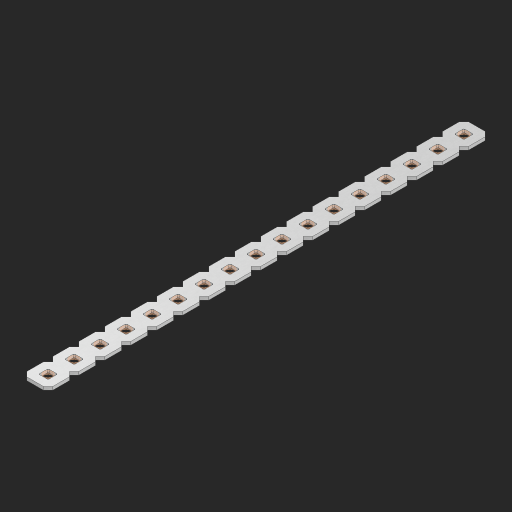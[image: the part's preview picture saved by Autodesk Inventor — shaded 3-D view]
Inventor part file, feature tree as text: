
AUTODESK INVENTOR PART (.ipt)
format: ipt  version: 2023 (Build 270158000, 158)  size: 450,560 bytes
history: native  units: in
note: dims shown in document units (in); Inventor stores cm internally (conversion verified against a paired STEP export)
features: other x18, extrude x16, sketch x2, pattern_linear x1
ambient origin geometry x8: Origin, YZ Plane, XZ Plane, XY Plane, X Axis, Y Axis, Z Axis, Center Point
bodies: Solid1 (feature_tree), Body (feature_tree)
feature tree (37):
  pattern_linear  "Rectangular Pattern1"  Spacing1=0.09in  [1 undecoded]
  sketch  "Sketch1"  dims[d1=0.5in]
  sketch  "Sketch2"  dims[d2=0.182in d3=0.09in d4=0.09in d5=0.09in d6=0.09in d7=0.09in d8=0.09in d9=0.09in d10=0.09in d11=0.02in d13=0.0in d14=0.172in d15=0.0625in d16=0.0in d19=0.5in d22=0.5in]
  other  "Srf1"
  other  "Srf126"
  other  "Srf127"
  other  "Srf128"
  other  "Srf129"
  other  "Srf130"
  other  "Srf131"
  other  "Srf250"
  other  "Srf251"
  other  "Srf252"
  other  "Srf253"
  other  "Srf254"
  other  "Srf255"
  other  "Srf256"
  other  "Srf257"
  other  "Srf258"
  other  "Srf259"
  other  "Circle"
  extrude  "ExtrusionSrf126"  Depth=0.09in
  extrude  "ExtrusionSrf127"  Depth=0.09in
  extrude  "ExtrusionSrf128"  Depth=0.09in
  extrude  "ExtrusionSrf129"  Depth=0.09in
  extrude  "ExtrusionSrf130"  Depth=0.09in
  extrude  "ExtrusionSrf131"  Depth=0.09in
  extrude  "ExtrusionSrf250"  Depth=0.09in
  extrude  "ExtrusionSrf251"  Depth=0.02in
  extrude  "ExtrusionSrf252"  TaperAngle=0.0deg  [1 undecoded]
  extrude  "ExtrusionSrf253"  Depth=0.5in
  extrude  "ExtrusionSrf254"  Depth=0.0625in TaperAngle=0.0deg
  extrude  "ExtrusionSrf255"  Depth=0.5in
  extrude  "ExtrusionSrf256"  Depth=0.5in
  extrude  "ExtrusionSrf257"  [1 undecoded]
  extrude  "ExtrusionSrf258"  [1 undecoded]
  extrude  "ExtrusionSrf259"  [1 undecoded]
note: 5 required parameter values undecoded (feature->parameter linkage not recoverable at this tier; creation-order binding heuristic only, values carry confidence <= 0.55)
